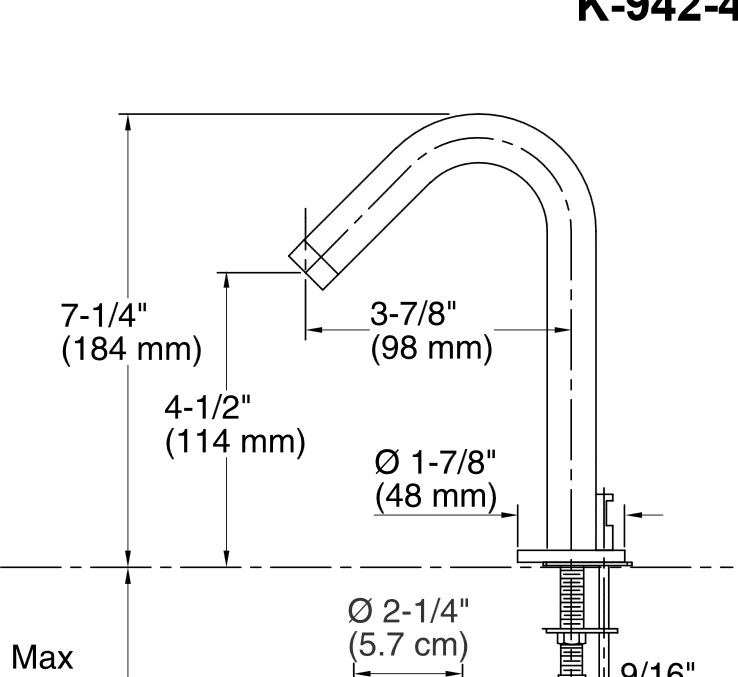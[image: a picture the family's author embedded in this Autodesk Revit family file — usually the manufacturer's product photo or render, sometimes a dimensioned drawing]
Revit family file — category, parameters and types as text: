
# Revit family: Faucet-Counter_Mount-Kohler-Stillness-K_942-4
name_source: partatom
category: Plumbing Fixtures
revit_build: Autodesk Revit 2015 (Build: 20140606_1530(x64)
units: mm (PartAtom-declared; Revit-internal decimal feet)

## types (2) — shared parameters
ADA Compliant = Yes
Assembly Code = D2010
CW Connection = Yes
Cold Water Connector = Cold Water
Cold Water Diameter = 0' - 0 3/8"
Default Elevation = 2' - 10"
Flow Rate = 1 GPM
HW Connection = Yes
Handle Clearance = 0' - 2 1/8"
Height = 0' - 7 1/4"
Hot Water Connector = Hot Water
Hot Water Diameter = 0' - 0 3/8"
Keynote = 22 40 00
Length = 0' - 3 7/8"
Manufacturer = Kohler
Material = Brass
Pressure = 60.00 psi
Product Documentation Link = http://www.us.kohler.com
Product Name = Stillness Widespread Bathroom Sink Faucet With Lever Handles
Product Page URL = http://www.us.kohler.com
Spout Reach = 0' - 3 7/8"
URL = http://www.us.kohler.com
Vent Connection = No
Version = 2014 - v1.0a
Waste Connection = No
zero-valued in all types: CWFU, HWFU, WFU

## per-type parameters (varying)
| type | ControlM | Description | Finish | Model |
| BN - Vibrant Brushed Nickel | 6820 | Widespread Bathroom Sink Faucet, Vibrant Brushed Nickel | Metal - Kohler - SN - Vibrant Polished Nickel | K-942-4-BN |
| CP - Polished Chrome | 6914 | Widespread Bathroom Sink Faucet, Polished Chrome | Metal - Kohler - CP - Polished Chrome | K-942-4-CP |

## geometry (parser evidence)
native form markers: Sweep x6
no freeform markers — native parametric forms only
